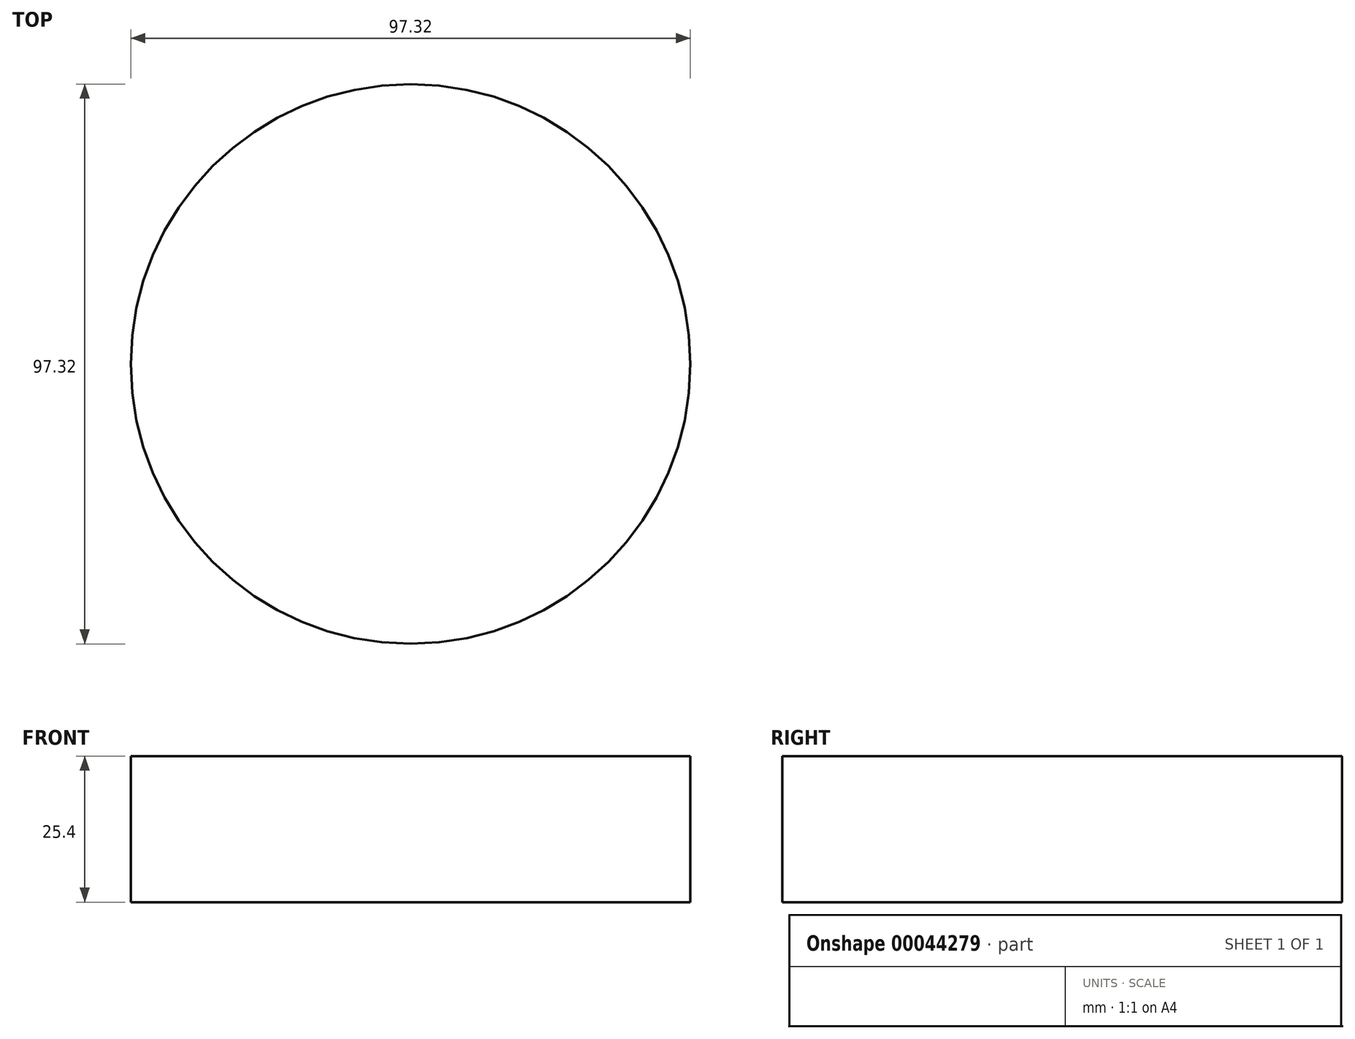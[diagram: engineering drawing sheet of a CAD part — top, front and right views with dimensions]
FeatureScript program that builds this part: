
annotation { "Feature Type Name" : "Feature", "Feature Type Description" : "" }
export const myFeature = defineFeature(function(context is Context, id is Id, definition is map)
    precondition{}
    {
        {
            var Q0;
            Q0=qCreatedBy(makeId("Top.planeOp"),FACE);
            var sketch = newSketch(context, id + "F0", { "sketchPlane" : qUnion([Q0])});
            skCircle(sketch, "E0", {"center": v(0, 0) * mm, "radius": 48.66 * mm});
            skSolve(sketch);
        }
        {
            var Q0;
            Q0 = qSketchRegion(id + "F0", true);
            extrude(context, id + "F1", {"entities" : qUnion([Q0]), "depth" : 25.4 * mm});
        }
        {
            var Q0;
            Q0=qCreatedBy(makeId("Top.planeOp"),FACE);
            var sketch = newSketch(context, id + "F2", { "sketchPlane" : qUnion([Q0])});
            skLineSegment(sketch, "E1.rect.bottom", {"start": v(-17.23, 14.03) * mm, "end": v(17.23, 14.03) * mm});
            skLineSegment(sketch, "E1.rect.top", {"start": v(-17.23, -14.03) * mm, "end": v(17.23, -14.03) * mm});
            skLineSegment(sketch, "E1.rect.left", {"start": v(-17.23, 14.03) * mm, "end": v(-17.23, -14.03) * mm});
            skLineSegment(sketch, "E1.rect.right", {"start": v(17.23, 14.03) * mm, "end": v(17.23, -14.03) * mm});
            skPoint(sketch, "E1.rect.middle", {"position": v(0, 0) * mm});
            skSolve(sketch);
        }
        {
            var Q0;
            Q0 = qSketchRegion(id + "F2", true);
            extrude(context, id + "F3", {"entities" : qUnion([Q0]), "operationType" : NewBodyOperationType.ADD, "depth" : 25.4 * mm});
        }
    });
